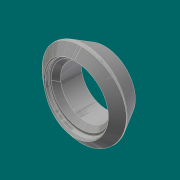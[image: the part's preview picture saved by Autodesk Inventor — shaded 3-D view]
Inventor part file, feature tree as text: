
AUTODESK INVENTOR PART (.ipt)
format: ipt  version: 2017.3 (Build 213257000, 257)  size: 358,912 bytes
history: native  units: mm (DEFAULTED — no unit token found)
features: other x7, sketch x5, plane x3, extrude x2, sweep x1, fillet x1
ambient origin geometry x8: Origin, YZ Plane, XZ Plane, XY Plane, X Axis, Y Axis, Z Axis, Center Point
bodies: Solid1 (feature_tree)
feature tree (19):
  sketch  "Sketch1"  dims[d5=44.45mm d8=90.0deg]
  plane  "Work Plane1"
  sketch  "Sketch2"  dims[d9=0.0mm d10=917.575mm]
  extrude  "Extrusion1"  TaperAngle=90.0deg  [1 undecoded]
  plane  "Work Plane2"
  sweep  "Sweep1"
  other  "Work Axis1"
  other  "Work Point1"
  other  "Work Point2"
  other  "Work Point3"
  plane  "Work Plane8"
  extrude  "Extrusion2"  [1 undecoded]
  fillet  "Fillet1"  Radius=73.66mm
  sketch  "Sketch3"  dims[d11=10.0mm d12=0.0mm d13=-503.2375mm d21=73.66mm]
  sketch  "3D Sketch1"
  other  "Edges3"
  other  "Edges4"
  other  "Work Axis2"
  sketch  "Sketch11"  dims[d22=6.0mm d23=4.0mm d24=2.0mm d25=90.0deg d26=30.1625mm d27=0.0mm d41=30.0deg d45=2.44475mm d50=39.37mm d51=44.45mm d52=122.2375mm d53=120.0deg d54=1191.41875mm d76=503.2375mm d77=0.0mm d79=2.19456mm d82=14.2875mm d83=8.290314mm d84=2.19456mm d85=0.0mm d86=0.0mm d87=90.0deg d88=0.0mm d89=90.0deg d90=93.6625mm d91=93.6625mm d92=0.0mm d93=-38.1mm d94=92.075mm d95=0.0mm d96=0.0mm d97=0.79375mm]
note: 2 required parameter values undecoded (feature->parameter linkage not recoverable at this tier; creation-order binding heuristic only, values carry confidence <= 0.55)
